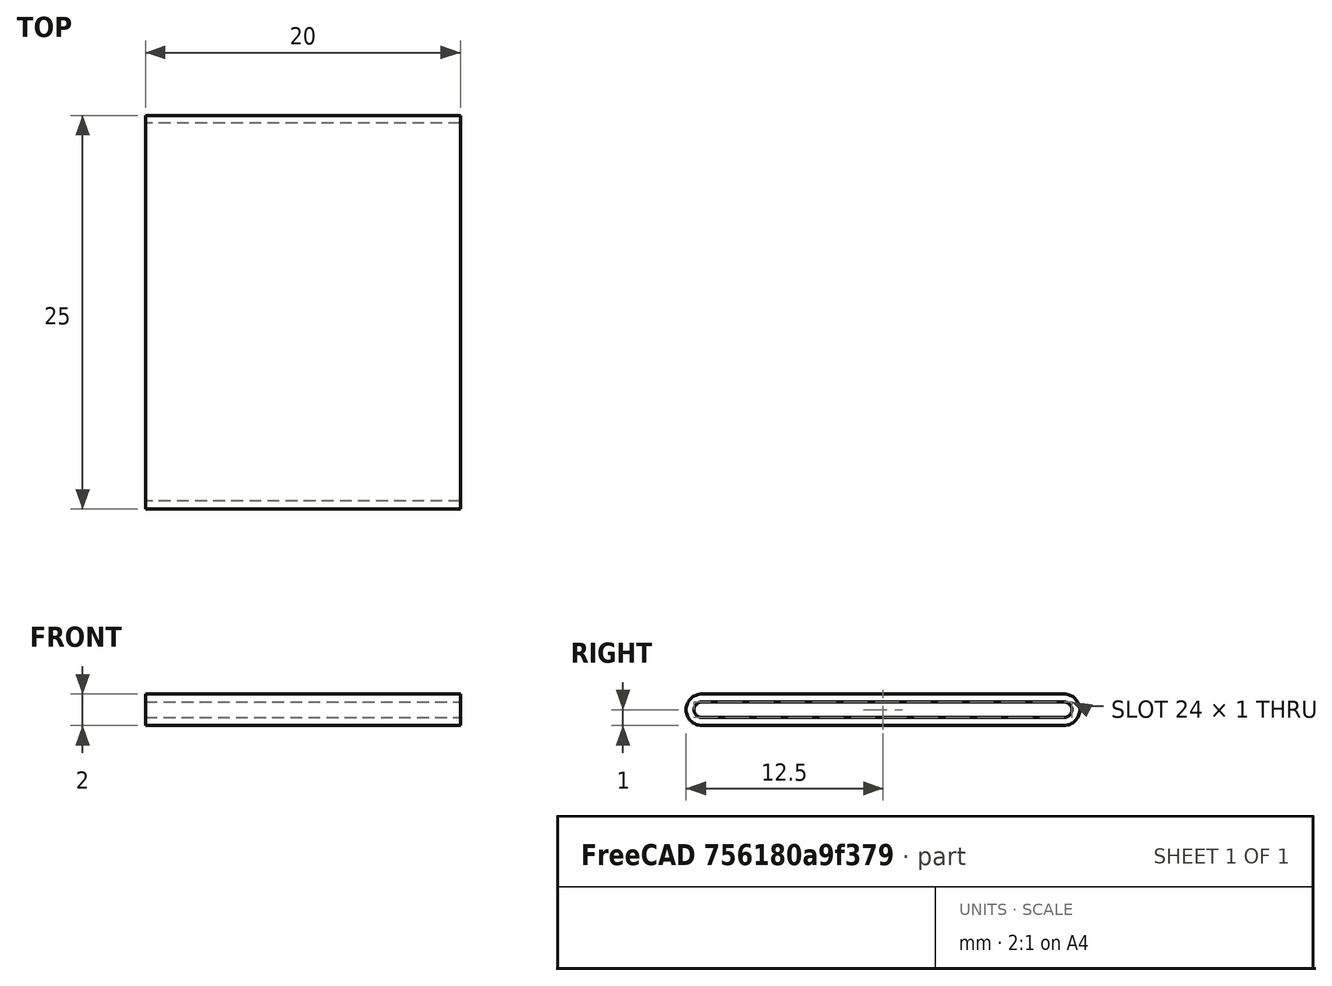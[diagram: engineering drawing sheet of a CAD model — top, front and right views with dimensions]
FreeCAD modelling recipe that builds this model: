
FCSTD DOCUMENT  (FreeCAD 0.20R29410 (Git))
Label: buckle
License: All rights reserved
LicenseURL: http://en.wikipedia.org/wiki/All_rights_reserved
objects: Sketcher::SketchObject×1, PartDesign::Pad×1, PartDesign::Body×1
note: 4 computed .brp shape members not serialized (recipe doc carries the construction recipe); baked Part::Feature solids carry a one-line shape summary decoded from their .brp

FEATURE [Sketcher::SketchObject] Sketch
  FullyConstrained = true
  MapMode = 5
  Placement = pos=(0,0,0) rot=(0.57735,0.57735,0.57735;2.0944rad)
  Support = -> [YZ_Plane]
  sketch-geometry (8):
    g0: LineSegment StartX=-23 StartY=-0.5 StartZ=0 EndX=0 EndY=-0.5 EndZ=0
    g1: LineSegment StartX=-23 StartY=0.5 StartZ=0 EndX=0 EndY=0.5 EndZ=0
    g2: ArcOfCircle CenterX=-23 CenterY=0 CenterZ=0 NormalX=0 NormalY=0 NormalZ=1 AngleXU=0 Radius=0.5 StartAngle=1.5708 EndAngle=4.71239
    g3: ArcOfCircle CenterX=4e-16 CenterY=0 CenterZ=0 NormalX=0 NormalY=0 NormalZ=1 AngleXU=0 Radius=0.5 StartAngle=4.71239 EndAngle=7.85398
    g4: LineSegment StartX=-23 StartY=-1 StartZ=0 EndX=0 EndY=-1 EndZ=0
    g5: LineSegment StartX=-23 StartY=1 StartZ=0 EndX=0 EndY=1 EndZ=0
    g6: ArcOfCircle CenterX=-23 CenterY=0 CenterZ=0 NormalX=0 NormalY=0 NormalZ=1 AngleXU=0 Radius=1 StartAngle=1.5708 EndAngle=4.71239
    g7: ArcOfCircle CenterX=4e-16 CenterY=0 CenterZ=0 NormalX=0 NormalY=0 NormalZ=1 AngleXU=0 Radius=1 StartAngle=4.71239 EndAngle=7.85398
  constraints (27):
    c: Horizontal(g0)
    c: Horizontal(g1)
    c: DistanceY(g0,g1) = 1
    c: Coincident(g2,g1)
    c: Coincident(g2,g0)
    c: Vertical(g1,g0)
    c: Coincident(g3,g1)
    c: Coincident(g3,g0)
    c: Vertical(g1,g0)
    c: Vertical(g2,g1)
    c: Vertical(g3,g1)
    c: Horizontal(g4)
    c: DistanceY(g4,g0) = 0.5
    c: Vertical(g4,g2)
    c: Vertical(g4,g3)
    c: DistanceX(g1,g1) = 23
    c: Horizontal(g5)
    c: Vertical(g5,g1)
    c: Vertical(g5,g1)
    c: DistanceY(g1,g5) = 0.5
    c: Coincident(g6,g4)
    c: Coincident(g6,g5)
    c: Vertical(g6,g5)
    c: Coincident(g7,g5)
    c: Coincident(g7,g4)
    c: Vertical(g7,g5)
    c: Coincident(g3,g-1)
FEATURE [PartDesign::Pad] Pad
  Direction = (1,-2e-16,3e-16)
  Length = 20
  Length2 = 10
  Placement = pos=(0,0,0) rot=(0.57735,0.57735,0.57735;2.0944rad)
  Profile = -> Sketch
  ReferenceAxis = -> Sketch [N_Axis]
  Type = 0
FEATURE [PartDesign::Body] Body
  Group = -> [Sketch,Pad]
  Origin = -> Origin
  Tip = -> Pad
